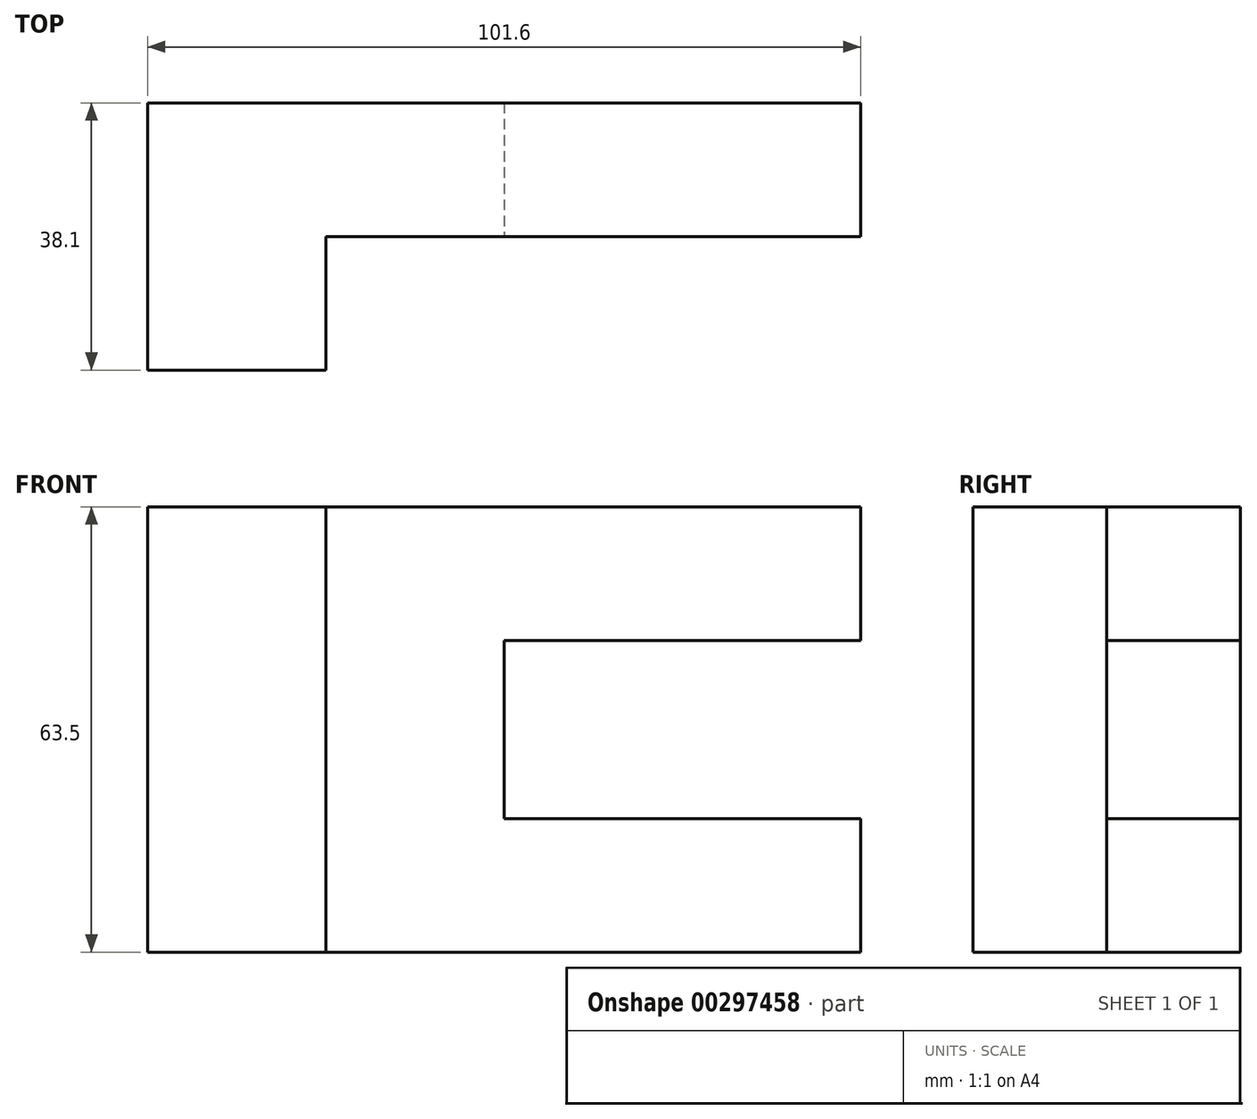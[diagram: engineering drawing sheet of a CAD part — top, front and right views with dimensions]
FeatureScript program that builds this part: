
annotation { "Feature Type Name" : "Feature", "Feature Type Description" : "" }
export const myFeature = defineFeature(function(context is Context, id is Id, definition is map)
    precondition{}
    {
        {
            var Q0;
            Q0=qCreatedBy(makeId("Front.planeOp"),FACE);
            var sketch = newSketch(context, id + "F0", { "sketchPlane" : qUnion([Q0])});
            skLineSegment(sketch, "E0.bottom", {"start": v(-50.8, 31.75) * mm, "end": v(50.8, 31.75) * mm});
            skLineSegment(sketch, "E0.top", {"start": v(-50.8, -31.75) * mm, "end": v(50.8, -31.75) * mm});
            skLineSegment(sketch, "E0.left", {"start": v(-50.8, 31.75) * mm, "end": v(-50.8, -31.75) * mm});
            skLineSegment(sketch, "E0.right", {"start": v(50.8, 31.75) * mm, "end": v(50.8, -31.75) * mm});
            skPoint(sketch, "E0.middle", {"position": v(0, 0) * mm});
            skSolve(sketch);
        }
        {
            var Q0;
            Q0 = qSketchRegion(id + "F0", true);
            extrude(context, id + "F1", {"entities" : qUnion([Q0]), "depth" : 38.1 * mm});
        }
        {
            var Q0;
            Q0=makeQuery(id+"F1.opExtrude","CAP_FACE",FACE,{"disambiguationData":[OSD([sQuery(id+"F0.wireOp",EDGE,"E0.bottom"),sQuery(id+"F0.wireOp",EDGE,"E0.top"),sQuery(id+"F0.wireOp",EDGE,"E0.left"),sQuery(id+"F0.wireOp",EDGE,"E0.right")])],"isStart":false});
            var sketch = newSketch(context, id + "F2", { "sketchPlane" : qUnion([Q0])});
            skLineSegment(sketch, "E1.bottom", {"start": v(-25.4, 31.75) * mm, "end": v(50.8, 31.75) * mm});
            skLineSegment(sketch, "E1.top", {"start": v(-25.4, -31.75) * mm, "end": v(50.8, -31.75) * mm});
            skLineSegment(sketch, "E1.left", {"start": v(-25.4, 31.75) * mm, "end": v(-25.4, -31.75) * mm});
            skLineSegment(sketch, "E1.right", {"start": v(50.8, 31.75) * mm, "end": v(50.8, -31.75) * mm});
            skSolve(sketch);
        }
        {
            var Q0;
            Q0 = qSketchRegion(id + "F2", true);
            extrude(context, id + "F3", {"entities" : qUnion([Q0]), "operationType" : NewBodyOperationType.REMOVE, "oppositeDirection" : true, "depth" : 19.05 * mm});
        }
        {
            var Q0;
            Q0=makeQuery(id+"F3.boolean.opBoolean","COPY",FACE,{"derivedFrom":makeQuery(id+"F3.opExtrude","CAP_FACE",FACE,{"disambiguationData":[OSD([sQuery(id+"F2.wireOp",EDGE,"E1.bottom"),sQuery(id+"F2.wireOp",EDGE,"E1.top"),sQuery(id+"F2.wireOp",EDGE,"E1.left"),sQuery(id+"F2.wireOp",EDGE,"E1.right")])],"isStart":false})});
            var sketch = newSketch(context, id + "F4", { "sketchPlane" : qUnion([Q0])});
            skLineSegment(sketch, "E2.bottom", {"start": v(50.8, 12.7) * mm, "end": v(0, 12.7) * mm});
            skLineSegment(sketch, "E2.top", {"start": v(50.8, -12.7) * mm, "end": v(0, -12.7) * mm});
            skLineSegment(sketch, "E2.left", {"start": v(50.8, 12.7) * mm, "end": v(50.8, -12.7) * mm});
            skLineSegment(sketch, "E2.right", {"start": v(0, 12.7) * mm, "end": v(0, -12.7) * mm});
            skSolve(sketch);
        }
        {
            var Q0;
            Q0=makeQuery(id+"F4.imprint","IMPRINT",FACE,{"disambiguationData":[TD([[makeQuery(id+"F4.imprint","IMPRINT",EDGE,{"derivedFrom":sQuery(id+"F4.wireOp",EDGE,"E2.bottom")}),1.0]])]});
            extrude(context, id + "F5", {"entities" : qUnion([Q0]), "operationType" : NewBodyOperationType.REMOVE, "endBound" : BoundingType.THROUGH_ALL, "oppositeDirection" : true, "depth" : 25.4 * mm});
        }
    });
